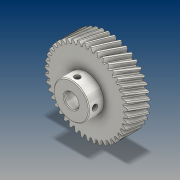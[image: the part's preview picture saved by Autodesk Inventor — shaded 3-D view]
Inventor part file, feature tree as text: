
AUTODESK INVENTOR PART (.ipt)
format: ipt  version: 2021 (Build 250183000, 183)  size: 923,136 bytes
history: native  units: mm (DEFAULTED — no unit token found)
features: extrude x4, sketch x4, plane x3, other x3, chamfer x2, projected_geometry x2, pattern_circular x1
ambient origin geometry x8: Origin, YZ Plane, XZ Plane, XY Plane, X Axis, Y Axis, Z Axis, Center Point
bodies: Solid1 (feature_tree)
feature tree (19):
  extrude  "Extrusion1"  Depth=15.0mm TaperAngle=0.0deg
  plane  "Work Plane2"
  plane  "Work Plane8"
  plane  "Work Plane9"
  other  "Spur Gear"
  sketch  "Sketch3"  dims[d16=45.0mm d17=0.0mm d34=0.747998mm]
  extrude  "Extrusion2"  Depth=10.0mm TaperAngle=0.0deg
  extrude  "Extrusion3"  Depth=0.747998mm TaperAngle=0.0deg
  extrude  "Extrusion4"  TaperAngle=0.0deg  [1 undecoded]
  pattern_circular  "Circular Pattern1"  [2 undecoded]
  chamfer  "Chamfer1"  Distance=45.0mm
  chamfer  "Chamfer2"  [1 undecoded]
  sketch  "Sketch1"  dims[d0=55.253778mm d1=15.0mm d2=0.0mm]
  sketch  "Sketch2"  dims[d3=55.869333mm d4=10.0mm d5=0.0mm]
  other  "Srf1"
  projected_geometry  "Projected Loop1"
  sketch  "Sketch4"  dims[d39=0.0mm d41=0.0mm d43=45.0mm d46=45.0mm d47=0.0mm d48=0.0mm d49=7.0mm d50=9.6mm d51=0.0mm d52=0.0mm d53=10.0mm d54=0.0mm d55=4.0mm d56=3.8mm d57=0.0mm d58=0.0mm d59=20.0mm d60=90.0deg d62=0.5mm d63=2.0mm d64=45.0deg d65=0.5mm d66=2.0mm d67=45.0deg]
  projected_geometry  "Projected Loop2"
  other  "Pitch Diameter"
note: 4 required parameter values undecoded (feature->parameter linkage not recoverable at this tier; creation-order binding heuristic only, values carry confidence <= 0.55)
